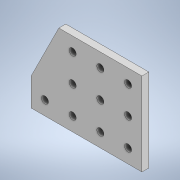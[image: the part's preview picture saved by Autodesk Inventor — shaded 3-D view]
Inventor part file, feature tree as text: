
AUTODESK INVENTOR PART (.ipt)
format: ipt  version: 2020 (Build 240168000, 168)  size: 119,808 bytes
history: native  units: in
note: dims shown in document units (in); Inventor stores cm internally (conversion verified against a paired STEP export)
features: extrude x1, sketch x1
ambient origin geometry x8: Origin, YZ Plane, XZ Plane, XY Plane, X Axis, Y Axis, Z Axis, Center Point
bodies: Solid1 (feature_tree)
feature tree (2):
  extrude  "Extrusion1"  Depth=3.0in
  sketch  "Sketch1"  dims[d0=4.0in d1=3.0in d2=3.0in d3=1.0in d4=0.256in d5=0.5in d6=0.5in d7=1.5748in d9=1.0in d10=0.3937in d12=1.0in d14=1.1811in d16=1.0in d17=0.3937in d19=1.0in d21=0.25in d22=0.0in]
